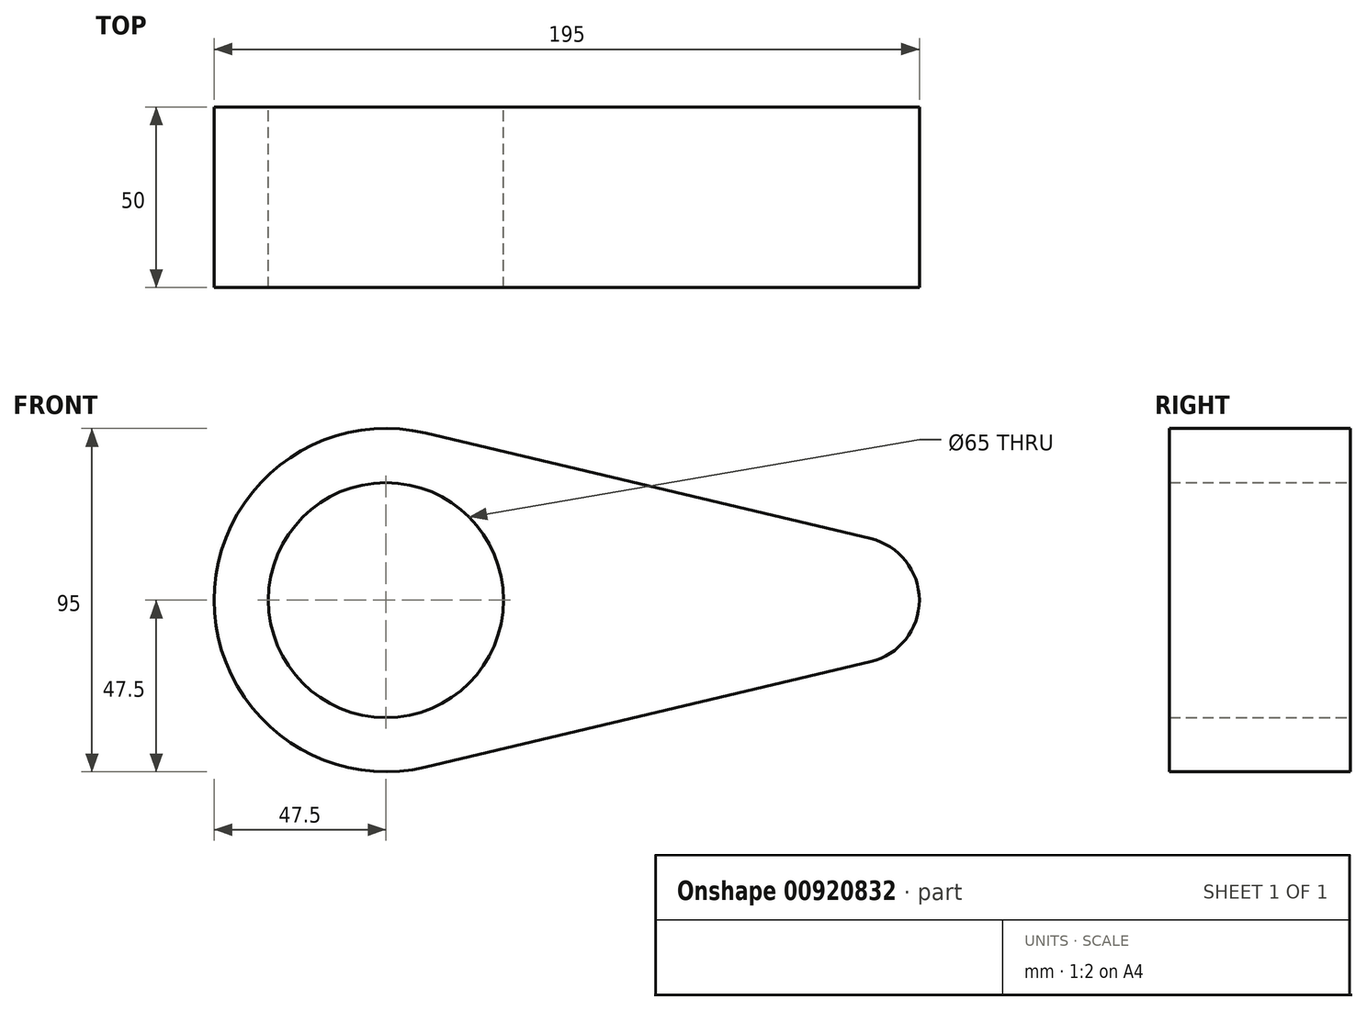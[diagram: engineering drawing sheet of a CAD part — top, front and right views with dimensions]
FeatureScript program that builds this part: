
annotation { "Feature Type Name" : "Feature", "Feature Type Description" : "" }
export const myFeature = defineFeature(function(context is Context, id is Id, definition is map)
    precondition{}
    {
        {
            var Q0;
            Q0=qCreatedBy(makeId("Front.planeOp"),FACE);
            var sketch = newSketch(context, id + "F0", { "sketchPlane" : qUnion([Q0])});
            skCircle(sketch, "E0", {"center": v(0, 0) * mm, "radius": 47.5 * mm});
            skCircle(sketch, "E1", {"center": v(130, 0) * mm, "radius": 17.5 * mm});
            skLineSegment(sketch, "E2", {"start": v(10.96, 46.22) * mm, "end": v(134.04, 17.03) * mm});
            skLineSegment(sketch, "E3", {"start": v(10.96, -46.22) * mm, "end": v(134.04, -17.03) * mm});
            skCircle(sketch, "E4", {"center": v(0, 0) * mm, "radius": 32.5 * mm});
            skSolve(sketch);
        }
        {
            var Q0;
            Q0 = qSketchRegion(id + "F0", true);
            extrude(context, id + "F1", {"entities" : qUnion([Q0]), "depth" : 50 * mm, "offsetDistance" : 25 * mm});
        }
    });
